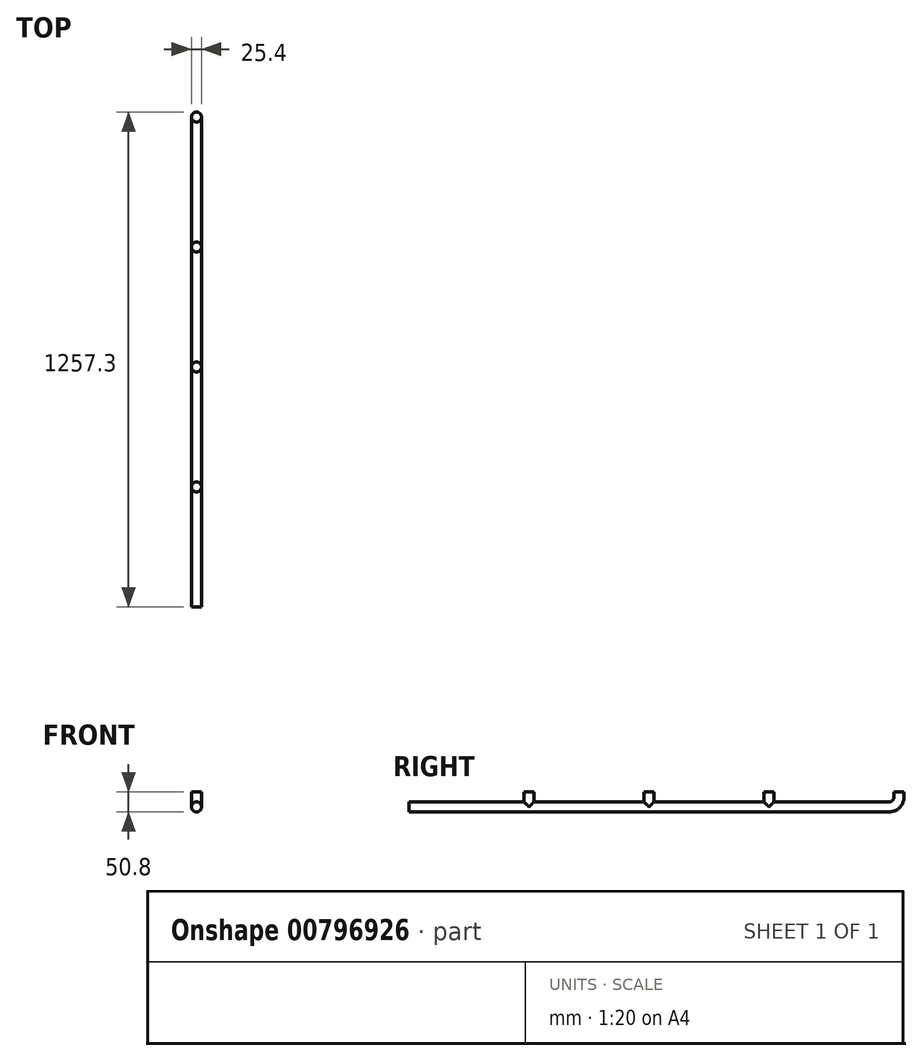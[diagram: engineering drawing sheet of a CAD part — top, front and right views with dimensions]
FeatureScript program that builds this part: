
annotation { "Feature Type Name" : "Feature", "Feature Type Description" : "" }
export const myFeature = defineFeature(function(context is Context, id is Id, definition is map)
    precondition{}
    {
        {
            var Q0;
            Q0=qCreatedBy(makeId("Front.planeOp"),FACE);
            var sketch = newSketch(context, id + "F0", { "sketchPlane" : qUnion([Q0])});
            skCircle(sketch, "E0", {"center": v(0, 0) * mm, "radius": 12.7 * mm});
            skSolve(sketch);
        }
        {
            var Q0;
            Q0 = qSketchRegion(id + "F0", true);
            extrude(context, id + "F1", {"entities" : qUnion([Q0]), "depth" : 609.6 * mm, "offsetDistance" : 25.4 * mm, "hasSecondDirection" : true, "secondDirectionOppositeDirection" : true, "secondDirectionDepth" : 609.6 * mm});
        }
        {
            var Q0;
            Q0=qCreatedBy(makeId("Top.planeOp"),FACE);
            cPlane(context, id + "F2", {"entities" : qUnion([Q0]), "cplaneType" : CPlaneType.OFFSET, "offset" : 38.1 * mm, "width" : 152.4 * mm, "height" : 152.4 * mm});
        }
        {
            var Q0;
            Q0=qCreatedBy(id+"F2.planeOp",FACE);
            var sketch = newSketch(context, id + "F3", { "sketchPlane" : qUnion([Q0])});
            skCircle(sketch, "E1", {"center": v(0, 635) * mm, "radius": 12.7 * mm});
            skSolve(sketch);
        }
        {
            var Q0;
            Q0=qCreatedBy(makeId("Right.planeOp"),FACE);
            var sketch = newSketch(context, id + "F4", { "sketchPlane" : qUnion([Q0])});
            skLineSegment(sketch, "E2", {"start": v(609.6, 0) * mm, "end": v(635, 0) * mm, "construction": true});
            skLineSegment(sketch, "E3", {"start": v(635, 0) * mm, "end": v(635, 25.4) * mm, "construction": true});
            skArc(sketch, "E4", {"start": v(635, 25.4) * mm, "mid": v(627.56, 7.44) * mm, "end": v(609.6, 0) * mm});
            skLineSegment(sketch, "E5", {"start": v(635, 25.4) * mm, "end": v(635, 38.1) * mm});
            skSolve(sketch);
        }
        {
            var Q0;
            Q0=makeQuery(id+"F3.imprint","IMPRINT",FACE,{"disambiguationData":[TD([[makeQuery(id+"F3.imprint","IMPRINT",EDGE,{"derivedFrom":sQuery(id+"F3.wireOp",EDGE,"E1")}),1.0]])]});
            var Q1;
            Q1=sQuery(id+"F4.wireOp",EDGE,"E4");
            var Q2;
            Q2=sQuery(id+"F4.wireOp",EDGE,"E5");
            sweep(context, id + "F5", {"operationType" : NewBodyOperationType.ADD, "profiles" : qUnion([Q0]), "path" : qUnion([Q1, Q2])});
        }
        {
            var Q0;
            Q0=qCreatedBy(makeId("Front.planeOp"),FACE);
            cPlane(context, id + "F6", {"entities" : qUnion([Q0]), "cplaneType" : CPlaneType.OFFSET, "offset" : 304.8 * mm, "width" : 152.4 * mm, "height" : 152.4 * mm});
        }
        {
            var Q0;
            Q0=qCreatedBy(makeId("Front.planeOp"),FACE);
            cPlane(context, id + "F7", {"entities" : qUnion([Q0]), "cplaneType" : CPlaneType.OFFSET, "offset" : 304.8 * mm, "oppositeDirection" : true, "width" : 152.4 * mm, "height" : 152.4 * mm});
        }
        {
            var Q0;
            Q0=qCreatedBy(id+"F2.planeOp",FACE);
            var sketch = newSketch(context, id + "F8", { "sketchPlane" : qUnion([Q0])});
            skCircle(sketch, "E6", {"center": v(0, 304.8) * mm, "radius": 12.7 * mm});
            skCircle(sketch, "E7", {"center": v(0, -304.8) * mm, "radius": 12.7 * mm});
            skCircle(sketch, "E8", {"center": v(0, 0) * mm, "radius": 12.7 * mm});
            skSolve(sketch);
        }
        {
            var Q0;
            Q0 = qSketchRegion(id + "F8", true);
            extrude(context, id + "F9", {"entities" : qUnion([Q0]), "operationType" : NewBodyOperationType.ADD, "endBound" : BoundingType.UP_TO_NEXT, "oppositeDirection" : true, "depth" : 25.4 * mm, "offsetDistance" : 25.4 * mm});
        }
    });
